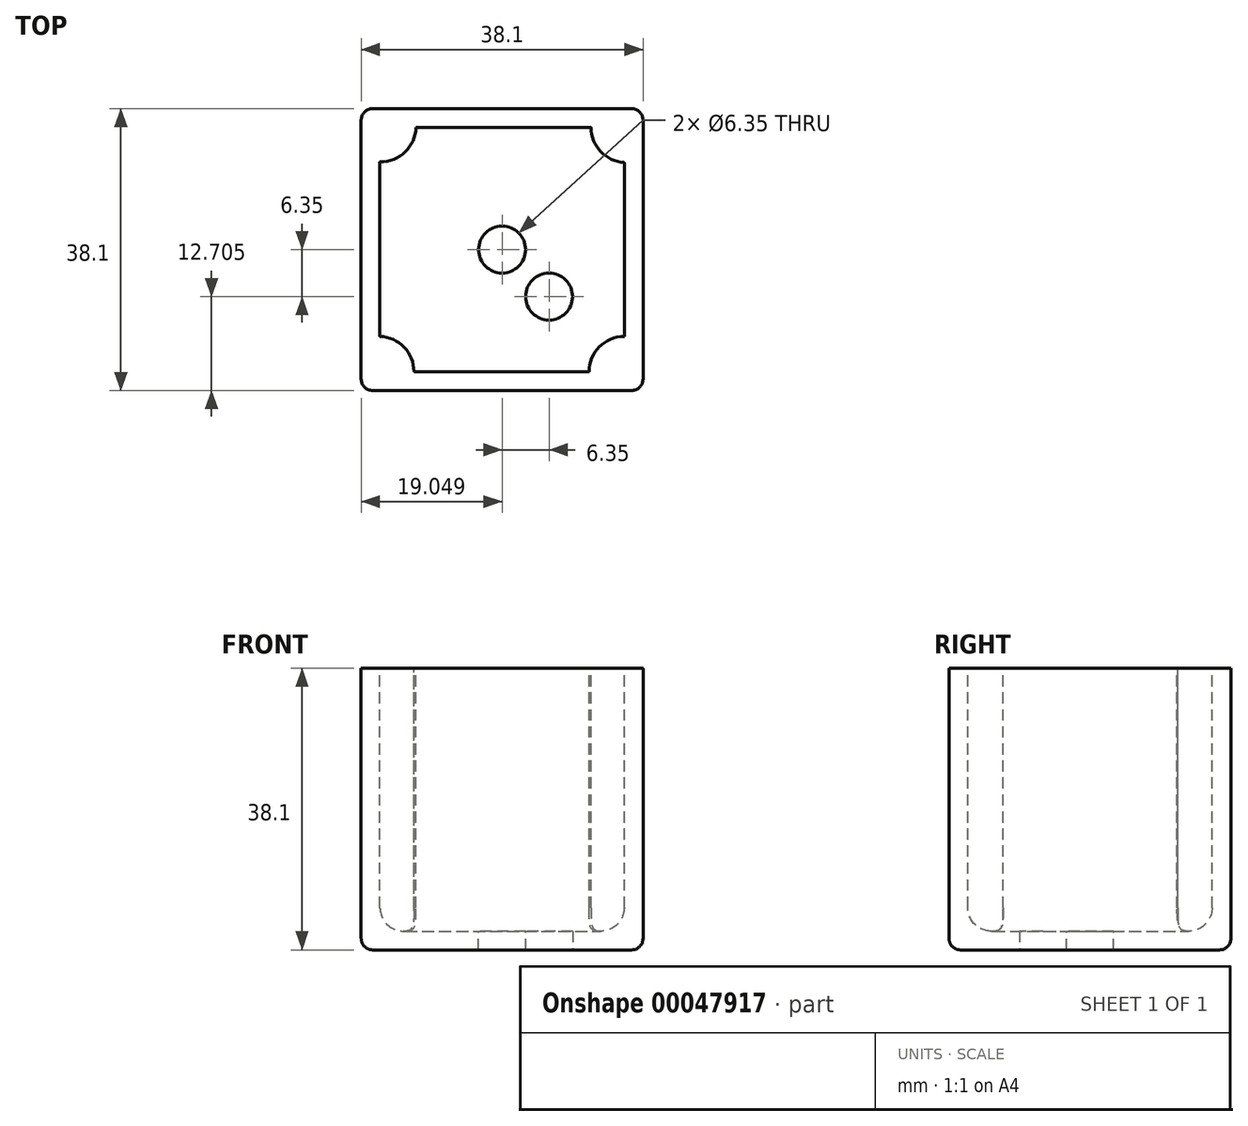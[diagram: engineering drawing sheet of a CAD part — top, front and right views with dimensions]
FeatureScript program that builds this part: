
annotation { "Feature Type Name" : "Feature", "Feature Type Description" : "" }
export const myFeature = defineFeature(function(context is Context, id is Id, definition is map)
    precondition{}
    {
        {
            var Q0;
            Q0=qCreatedBy(makeId("Top.planeOp"),FACE);
            var sketch = newSketch(context, id + "F0", { "sketchPlane" : qUnion([Q0])});
            skLineSegment(sketch, "E0.bottom", {"start": v(-10.73, -13.63) * mm, "end": v(27.37, -13.63) * mm});
            skLineSegment(sketch, "E0.top", {"start": v(-10.73, 24.47) * mm, "end": v(27.37, 24.47) * mm});
            skLineSegment(sketch, "E0.left", {"start": v(-10.73, -13.63) * mm, "end": v(-10.73, 24.47) * mm});
            skLineSegment(sketch, "E0.right", {"start": v(27.37, -13.63) * mm, "end": v(27.37, 24.47) * mm});
            skSolve(sketch);
        }
        {
            var Q0;
            Q0 = qSketchRegion(id + "F0", true);
            extrude(context, id + "F1", {"entities" : qUnion([Q0]), "depth" : 38.1 * mm});
        }
        {
            var Q0;
            Q0=makeQuery(id+"F1.opExtrude","CAP_FACE",FACE,{"disambiguationData":[OSD([sQuery(id+"F0.wireOp",EDGE,"E0.bottom"),sQuery(id+"F0.wireOp",EDGE,"E0.top"),sQuery(id+"F0.wireOp",EDGE,"E0.left"),sQuery(id+"F0.wireOp",EDGE,"E0.right")])],"isStart":false});
            shell(context, id + "F2", {"entities" : qUnion([Q0]), "thickness" : 2.54 * mm});
        }
        {
            var Q0;
            Q0=makeQuery(id+"F1.opExtrude","CAP_FACE",FACE,{"disambiguationData":[OSD([sQuery(id+"F0.wireOp",EDGE,"E0.bottom"),sQuery(id+"F0.wireOp",EDGE,"E0.top"),sQuery(id+"F0.wireOp",EDGE,"E0.left"),sQuery(id+"F0.wireOp",EDGE,"E0.right")])],"isStart":true});
            var sketch = newSketch(context, id + "F3", { "sketchPlane" : qUnion([Q0])});
            skPoint(sketch, "E1", {"position": v(8.32, -5.42) * mm});
            skSolve(sketch);
        }
        {
            var Q0;
            Q0=sQuery(id+"F3.wireOp",VERTEX,"E1");
            var Q1;
            Q1=makeQuery(id+"F1.opExtrude","SWEPT_BODY",BODY,{"disambiguationData":[OSD([sQuery(id+"F0.wireOp",EDGE,"E0.bottom"),sQuery(id+"F0.wireOp",EDGE,"E0.top"),sQuery(id+"F0.wireOp",EDGE,"E0.left"),sQuery(id+"F0.wireOp",EDGE,"E0.right")])]});
            hole(context, id + "F4", {"style" : HoleStyle.SIMPLE, "holeDiameter" : 6.35 * mm, "endStyle" : HoleEndStyle.THROUGH, "locations" : qUnion([Q0]), "scope" : qUnion([Q1])});
        }
        {
            var Q0;
            Q0=makeQuery(id+"F1.opExtrude","CAP_EDGE",EDGE,{"disambiguationData":[OSD([sQuery(id+"F0.wireOp",EDGE,"E0.bottom")])],"isStart":true});
            var Q1;
            Q1=makeQuery(id+"F1.opExtrude","CAP_EDGE",EDGE,{"disambiguationData":[OSD([sQuery(id+"F0.wireOp",EDGE,"E0.left")])],"isStart":true});
            var Q2;
            Q2=makeQuery(id+"F1.opExtrude","CAP_EDGE",EDGE,{"disambiguationData":[OSD([sQuery(id+"F0.wireOp",EDGE,"E0.right")])],"isStart":true});
            var Q3;
            Q3=makeQuery(id+"F1.opExtrude","CAP_EDGE",EDGE,{"disambiguationData":[OSD([sQuery(id+"F0.wireOp",EDGE,"E0.top")])],"isStart":true});
            var Q4;
            Q4=makeQuery(id+"F1.opExtrude","SWEPT_EDGE",EDGE,{"disambiguationData":[OSD([sQuery(id+"F0.wireOp",EDGE,"E0.top"),sQuery(id+"F0.wireOp",EDGE,"E0.right")])]});
            var Q5;
            Q5=makeQuery(id+"F1.opExtrude","SWEPT_EDGE",EDGE,{"disambiguationData":[OSD([sQuery(id+"F0.wireOp",EDGE,"E0.bottom"),sQuery(id+"F0.wireOp",EDGE,"E0.right")])]});
            var Q6;
            Q6=makeQuery(id+"F1.opExtrude","SWEPT_EDGE",EDGE,{"disambiguationData":[OSD([sQuery(id+"F0.wireOp",EDGE,"E0.top"),sQuery(id+"F0.wireOp",EDGE,"E0.left")])]});
            var Q7;
            Q7=makeQuery(id+"F1.opExtrude","SWEPT_EDGE",EDGE,{"disambiguationData":[OSD([sQuery(id+"F0.wireOp",EDGE,"E0.bottom"),sQuery(id+"F0.wireOp",EDGE,"E0.left")])]});
            fillet(context, id + "F5", {"entities" : qUnion([Q0, Q1, Q2, Q3, Q4, Q5, Q6, Q7]), "radius" : 1.56 * mm, "tangentPropagation" : true, "allowEdgeOverflow" : false});
        }
        {
            var Q0;
            Q0=makeQuery(id+"F1.opExtrude","CAP_FACE",FACE,{"disambiguationData":[OSD([sQuery(id+"F0.wireOp",EDGE,"E0.bottom"),sQuery(id+"F0.wireOp",EDGE,"E0.top"),sQuery(id+"F0.wireOp",EDGE,"E0.left"),sQuery(id+"F0.wireOp",EDGE,"E0.right")])],"isStart":false});
            var sketch = newSketch(context, id + "F6", { "sketchPlane" : qUnion([Q0])});
            skArc(sketch, "E2", {"start": v(24.83, -6.32) * mm, "mid": v(21.46, -7.72) * mm, "end": v(20.07, -11.09) * mm});
            skArc(sketch, "E3", {"start": v(20.33, 21.93) * mm, "mid": v(21.64, 18.67) * mm, "end": v(24.83, 17.2) * mm});
            skArc(sketch, "E4", {"start": v(-8.2, 17.3) * mm, "mid": v(-4.8, 18.6) * mm, "end": v(-3.32, 21.93) * mm});
            skArc(sketch, "E5", {"start": v(-3.6, -11.09) * mm, "mid": v(-4.93, -7.76) * mm, "end": v(-8.2, -6.3) * mm});
            skPoint(sketch, "E6.orphan", {"position": v(-8.2, -11.09) * mm});
            skPoint(sketch, "E7.orphan", {"position": v(24.83, 21.93) * mm});
            skPoint(sketch, "E8.orphan", {"position": v(-8.2, 21.93) * mm});
            skLineSegment(sketch, "E9.0", {"start": v(24.83, -11.09) * mm, "end": v(24.83, -6.32) * mm});
            skLineSegment(sketch, "E10.1", {"start": v(-8.2, -11.09) * mm, "end": v(-3.6, -11.09) * mm});
            skLineSegment(sketch, "E10.2", {"start": v(-8.2, -11.09) * mm, "end": v(-8.2, -6.3) * mm});
            skLineSegment(sketch, "E10.3", {"start": v(-8.2, 21.93) * mm, "end": v(-3.32, 21.93) * mm});
            skLineSegment(sketch, "E11.trimOffspring", {"start": v(20.07, -11.09) * mm, "end": v(24.83, -11.09) * mm});
            skLineSegment(sketch, "E12.trimOffspring", {"start": v(24.83, 17.2) * mm, "end": v(24.83, 21.93) * mm});
            skLineSegment(sketch, "E13.trimOffspring", {"start": v(20.33, 21.93) * mm, "end": v(24.83, 21.93) * mm});
            skLineSegment(sketch, "E14.trimOffspring", {"start": v(-8.2, 17.3) * mm, "end": v(-8.2, 21.93) * mm});
            skSolve(sketch);
        }
        {
            var Q0;
            Q0 = qSketchRegion(id + "F6", true);
            var Q1;
            Q1=makeQuery(id+"F2.opShell","OFFSET_FACE",FACE,{"disambiguationData":[OSD([sQuery(id+"F0.wireOp",EDGE,"E0.bottom"),sQuery(id+"F0.wireOp",EDGE,"E0.top"),sQuery(id+"F0.wireOp",EDGE,"E0.left"),sQuery(id+"F0.wireOp",EDGE,"E0.right")])]});
            extrude(context, id + "F7", {"entities" : qUnion([Q0]), "operationType" : NewBodyOperationType.ADD, "endBound" : BoundingType.UP_TO_SURFACE, "oppositeDirection" : true, "endBoundEntityFace" : qUnion([Q1]), "depth" : 25.4 * mm});
        }
        {
            var Q0;
            Q0=makeQuery(id+"F7.opExtrude","SWEPT_EDGE",EDGE,{"disambiguationData":[OSD([sQuery(id+"F0.wireOp",EDGE,"E0.right"),sQuery(id+"F6.wireOp",EDGE,"E3"),sQuery(id+"F6.wireOp",EDGE,"E12.trimOffspring")])]});
            var Q1;
            {var subQ0=sQuery(id+"F0.wireOp",EDGE,"E0.right");Q1=makeQuery(id+"F2.opShell","OFFSET_EDGE",EDGE,{"disambiguationData":[OSD([subQ0]),TDD([makeQuery(id+"F1.opExtrude","CAP_EDGE",EDGE,{"disambiguationData":[OSD([subQ0])],"isStart":true})])]});}
            var Q2;
            Q2=makeQuery(id+"F7.opExtrude","CAP_EDGE",EDGE,{"disambiguationData":[OSD([sQuery(id+"F6.wireOp",EDGE,"E3")])],"isStart":false});
            var Q3;
            Q3=makeQuery(id+"F7.opExtrude","SWEPT_EDGE",EDGE,{"disambiguationData":[OSD([sQuery(id+"F0.wireOp",EDGE,"E0.top"),sQuery(id+"F6.wireOp",EDGE,"E3"),sQuery(id+"F6.wireOp",EDGE,"E13.trimOffspring")])]});
            var Q4;
            {var subQ0=sQuery(id+"F0.wireOp",EDGE,"E0.top");Q4=makeQuery(id+"F2.opShell","OFFSET_EDGE",EDGE,{"disambiguationData":[OSD([subQ0]),TDD([makeQuery(id+"F1.opExtrude","CAP_EDGE",EDGE,{"disambiguationData":[OSD([subQ0])],"isStart":true})])]});}
            var Q5;
            Q5=makeQuery(id+"F7.opExtrude","SWEPT_EDGE",EDGE,{"disambiguationData":[OSD([sQuery(id+"F0.wireOp",EDGE,"E0.right"),sQuery(id+"F6.wireOp",EDGE,"E2"),sQuery(id+"F6.wireOp",EDGE,"E9.0")])]});
            var Q6;
            Q6=makeQuery(id+"F7.opExtrude","CAP_EDGE",EDGE,{"disambiguationData":[OSD([sQuery(id+"F6.wireOp",EDGE,"E2")])],"isStart":false});
            var Q7;
            Q7=makeQuery(id+"F7.opExtrude","SWEPT_EDGE",EDGE,{"disambiguationData":[OSD([sQuery(id+"F0.wireOp",EDGE,"E0.bottom"),sQuery(id+"F6.wireOp",EDGE,"E2"),sQuery(id+"F6.wireOp",EDGE,"E11.trimOffspring")])]});
            var Q8;
            {var subQ0=sQuery(id+"F0.wireOp",EDGE,"E0.bottom");Q8=makeQuery(id+"F2.opShell","OFFSET_EDGE",EDGE,{"disambiguationData":[OSD([subQ0]),TDD([makeQuery(id+"F1.opExtrude","CAP_EDGE",EDGE,{"disambiguationData":[OSD([subQ0])],"isStart":true})])]});}
            var Q9;
            Q9=makeQuery(id+"F7.opExtrude","CAP_EDGE",EDGE,{"disambiguationData":[OSD([sQuery(id+"F6.wireOp",EDGE,"E5")])],"isStart":false});
            var Q10;
            Q10=makeQuery(id+"F7.opExtrude","SWEPT_EDGE",EDGE,{"disambiguationData":[OSD([sQuery(id+"F0.wireOp",EDGE,"E0.left"),sQuery(id+"F6.wireOp",EDGE,"E5"),sQuery(id+"F6.wireOp",EDGE,"E10.2")])]});
            var Q11;
            Q11=makeQuery(id+"F7.opExtrude","SWEPT_EDGE",EDGE,{"disambiguationData":[OSD([sQuery(id+"F0.wireOp",EDGE,"E0.bottom"),sQuery(id+"F6.wireOp",EDGE,"E5"),sQuery(id+"F6.wireOp",EDGE,"E10.1")])]});
            var Q12;
            Q12=makeQuery(id+"F7.opExtrude","CAP_EDGE",EDGE,{"disambiguationData":[OSD([sQuery(id+"F6.wireOp",EDGE,"E4")])],"isStart":false});
            var Q13;
            Q13=makeQuery(id+"F7.opExtrude","SWEPT_EDGE",EDGE,{"disambiguationData":[OSD([sQuery(id+"F0.wireOp",EDGE,"E0.left"),sQuery(id+"F6.wireOp",EDGE,"E4"),sQuery(id+"F6.wireOp",EDGE,"E14.trimOffspring")])]});
            var Q14;
            {var subQ0=sQuery(id+"F0.wireOp",EDGE,"E0.left");Q14=makeQuery(id+"F2.opShell","OFFSET_EDGE",EDGE,{"disambiguationData":[OSD([subQ0]),TDD([makeQuery(id+"F1.opExtrude","CAP_EDGE",EDGE,{"disambiguationData":[OSD([subQ0])],"isStart":true})])]});}
            var Q15;
            Q15=makeQuery(id+"F7.opExtrude","SWEPT_EDGE",EDGE,{"disambiguationData":[OSD([sQuery(id+"F0.wireOp",EDGE,"E0.top"),sQuery(id+"F6.wireOp",EDGE,"E4"),sQuery(id+"F6.wireOp",EDGE,"E10.3")])]});
            fillet(context, id + "F8", {"entities" : qUnion([Q0, Q1, Q2, Q3, Q4, Q5, Q6, Q7, Q8, Q9, Q10, Q11, Q12, Q13, Q14, Q15]), "radius" : 3.17 * mm, "tangentPropagation" : true, "allowEdgeOverflow" : false});
        }
        {
            var Q0;
            Q0=makeQuery(id+"F3.imprint","IMPRINT",FACE,{"disambiguationData":[TD([[makeQuery(id+"F3.imprint","IMPRINT",EDGE,{"derivedFrom":makeQuery(id+"F1.opExtrude","CAP_EDGE",EDGE,{"disambiguationData":[OSD([sQuery(id+"F0.wireOp",EDGE,"E0.bottom")])],"isStart":true})}),-1.0]])]});
            var sketch = newSketch(context, id + "F9", { "sketchPlane" : qUnion([Q0])});
            skCircle(sketch, "E15", {"center": v(14.67, 0.93) * mm, "radius": 3.17 * mm});
            skSolve(sketch);
        }
        {
            var Q0;
            Q0 = qSketchRegion(id + "F9", true);
            var Q1;
            Q1=sQuery(id+"F9.wireOp",EDGE,"E15");
            extrude(context, id + "F10", {"entities" : qUnion([Q0]), "operationType" : NewBodyOperationType.REMOVE, "surfaceEntities" : qUnion([Q1]), "endBound" : BoundingType.THROUGH_ALL, "oppositeDirection" : true, "depth" : 25.4 * mm});
        }
    });
